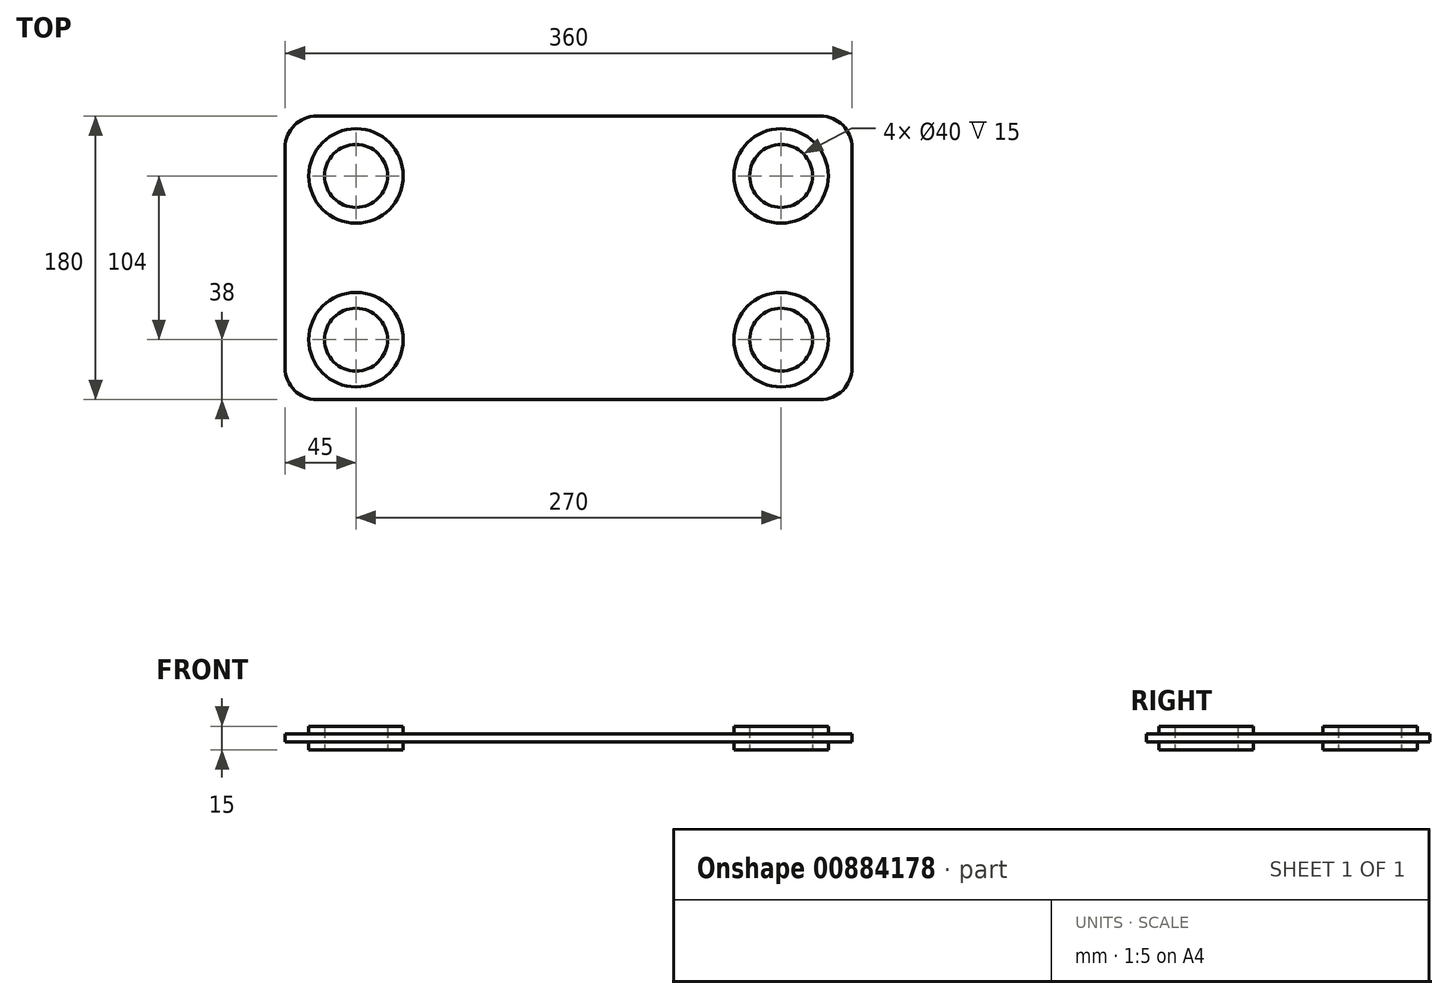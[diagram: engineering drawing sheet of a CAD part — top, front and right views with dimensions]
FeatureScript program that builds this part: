
annotation { "Feature Type Name" : "Feature", "Feature Type Description" : "" }
export const myFeature = defineFeature(function(context is Context, id is Id, definition is map)
    precondition{}
    {
        {
            var Q0;
            Q0=qCreatedBy(makeId("Top.planeOp"),FACE);
            var sketch = newSketch(context, id + "F0", { "sketchPlane" : qUnion([Q0])});
            skLineSegment(sketch, "E0.bottom", {"start": v(160, -90) * mm, "end": v(-160, -90) * mm});
            skLineSegment(sketch, "E0.top", {"start": v(160, 90) * mm, "end": v(-160, 90) * mm});
            skLineSegment(sketch, "E0.left", {"start": v(180, -70) * mm, "end": v(180, 70) * mm});
            skLineSegment(sketch, "E0.right", {"start": v(-180, -70) * mm, "end": v(-180, 70) * mm});
            skPoint(sketch, "E0.middle", {"position": v(0, 0) * mm});
            skLineSegment(sketch, "E1", {"start": v(0, -90) * mm, "end": v(0, 90) * mm, "construction": true});
            skLineSegment(sketch, "E2", {"start": v(-180, 0) * mm, "end": v(180, 0) * mm, "construction": true});
            skCircle(sketch, "E3", {"center": v(-135, -52) * mm, "radius": 20 * mm});
            skCircle(sketch, "E4.MirrorC", {"center": v(-135, 52) * mm, "radius": 20 * mm});
            skCircle(sketch, "E5.MirrorC", {"center": v(135, -52) * mm, "radius": 20 * mm});
            skCircle(sketch, "E6.MirrorC", {"center": v(135, 52) * mm, "radius": 20 * mm});
            skPoint(sketch, "E7.visualSharp", {"position": v(-180, 90) * mm});
            skArc(sketch, "E7.filletArc", {"start": v(-160, 90) * mm, "mid": v(-174.14, 84.14) * mm, "end": v(-180, 70) * mm});
            skPoint(sketch, "E8.visualSharp", {"position": v(180, 90) * mm});
            skArc(sketch, "E8.filletArc", {"start": v(180, 70) * mm, "mid": v(174.14, 84.14) * mm, "end": v(160, 90) * mm});
            skPoint(sketch, "E9.visualSharp", {"position": v(180, -90) * mm});
            skArc(sketch, "E9.filletArc", {"start": v(160, -90) * mm, "mid": v(174.14, -84.14) * mm, "end": v(180, -70) * mm});
            skPoint(sketch, "E10.visualSharp", {"position": v(-180, -90) * mm});
            skArc(sketch, "E10.filletArc", {"start": v(-180, -70) * mm, "mid": v(-174.14, -84.14) * mm, "end": v(-160, -90) * mm});
            skSolve(sketch);
        }
        {
            var Q0;
            Q0 = qSketchRegion(id + "F0", true);
            extrude(context, id + "F1", {"entities" : qUnion([Q0]), "depth" : 5 * mm, "offsetDistance" : 25 * mm});
        }
        {
            var Q0;
            Q0=makeQuery(id+"F1.opExtrude","CAP_FACE",FACE,{"disambiguationData":[OSD([sQuery(id+"F0.wireOp",EDGE,"E0.bottom"),sQuery(id+"F0.wireOp",EDGE,"E0.top"),sQuery(id+"F0.wireOp",EDGE,"E0.left"),sQuery(id+"F0.wireOp",EDGE,"E0.right"),sQuery(id+"F0.wireOp",EDGE,"E3"),sQuery(id+"F0.wireOp",EDGE,"E4.MirrorC"),sQuery(id+"F0.wireOp",EDGE,"E5.MirrorC"),sQuery(id+"F0.wireOp",EDGE,"E6.MirrorC")])],"isStart":false});
            var sketch = newSketch(context, id + "F2", { "sketchPlane" : qUnion([Q0])});
            skCircle(sketch, "E11", {"center": v(-135, 52) * mm, "radius": 20 * mm});
            skCircle(sketch, "E12", {"center": v(-135, 52) * mm, "radius": 30 * mm});
            skCircle(sketch, "E13.MirrorC", {"center": v(135, 52) * mm, "radius": 20 * mm});
            skCircle(sketch, "E14.MirrorC", {"center": v(135, 52) * mm, "radius": 30 * mm});
            skCircle(sketch, "E15.MirrorC", {"center": v(-135, -52) * mm, "radius": 20 * mm});
            skCircle(sketch, "E16.MirrorC", {"center": v(-135, -52) * mm, "radius": 30 * mm});
            skCircle(sketch, "E17.MirrorC", {"center": v(135, -52) * mm, "radius": 20 * mm});
            skCircle(sketch, "E18.MirrorC", {"center": v(135, -52) * mm, "radius": 30 * mm});
            skSolve(sketch);
        }
        {
            var Q0;
            Q0 = qSketchRegion(id + "F2", true);
            extrude(context, id + "F3", {"entities" : qUnion([Q0]), "operationType" : NewBodyOperationType.ADD, "depth" : 5 * mm, "offsetDistance" : 25 * mm});
        }
        {
            var Q0;
            Q0=makeQuery(id+"F1.opExtrude","CAP_FACE",FACE,{"disambiguationData":[OSD([sQuery(id+"F0.wireOp",EDGE,"E0.bottom"),sQuery(id+"F0.wireOp",EDGE,"E0.top"),sQuery(id+"F0.wireOp",EDGE,"E0.left"),sQuery(id+"F0.wireOp",EDGE,"E0.right"),sQuery(id+"F0.wireOp",EDGE,"E3"),sQuery(id+"F0.wireOp",EDGE,"E4.MirrorC"),sQuery(id+"F0.wireOp",EDGE,"E5.MirrorC"),sQuery(id+"F0.wireOp",EDGE,"E6.MirrorC")])],"isStart":true});
            var sketch = newSketch(context, id + "F4", { "sketchPlane" : qUnion([Q0])});
            skCircle(sketch, "E19", {"center": v(-135, 52) * mm, "radius": 20 * mm});
            skCircle(sketch, "E20", {"center": v(-135, 52) * mm, "radius": 30 * mm});
            skCircle(sketch, "E21.MirrorC", {"center": v(135, 52) * mm, "radius": 20 * mm});
            skCircle(sketch, "E22.MirrorC", {"center": v(135, 52) * mm, "radius": 30 * mm});
            skCircle(sketch, "E23.MirrorC", {"center": v(-135, -52) * mm, "radius": 20 * mm});
            skCircle(sketch, "E24.MirrorC", {"center": v(-135, -52) * mm, "radius": 30 * mm});
            skCircle(sketch, "E25.MirrorC", {"center": v(135, -52) * mm, "radius": 20 * mm});
            skCircle(sketch, "E26.MirrorC", {"center": v(135, -52) * mm, "radius": 30 * mm});
            skSolve(sketch);
        }
        {
            var Q0;
            Q0 = qSketchRegion(id + "F4", true);
            extrude(context, id + "F5", {"entities" : qUnion([Q0]), "operationType" : NewBodyOperationType.ADD, "depth" : 5 * mm, "offsetDistance" : 25 * mm});
        }
    });
